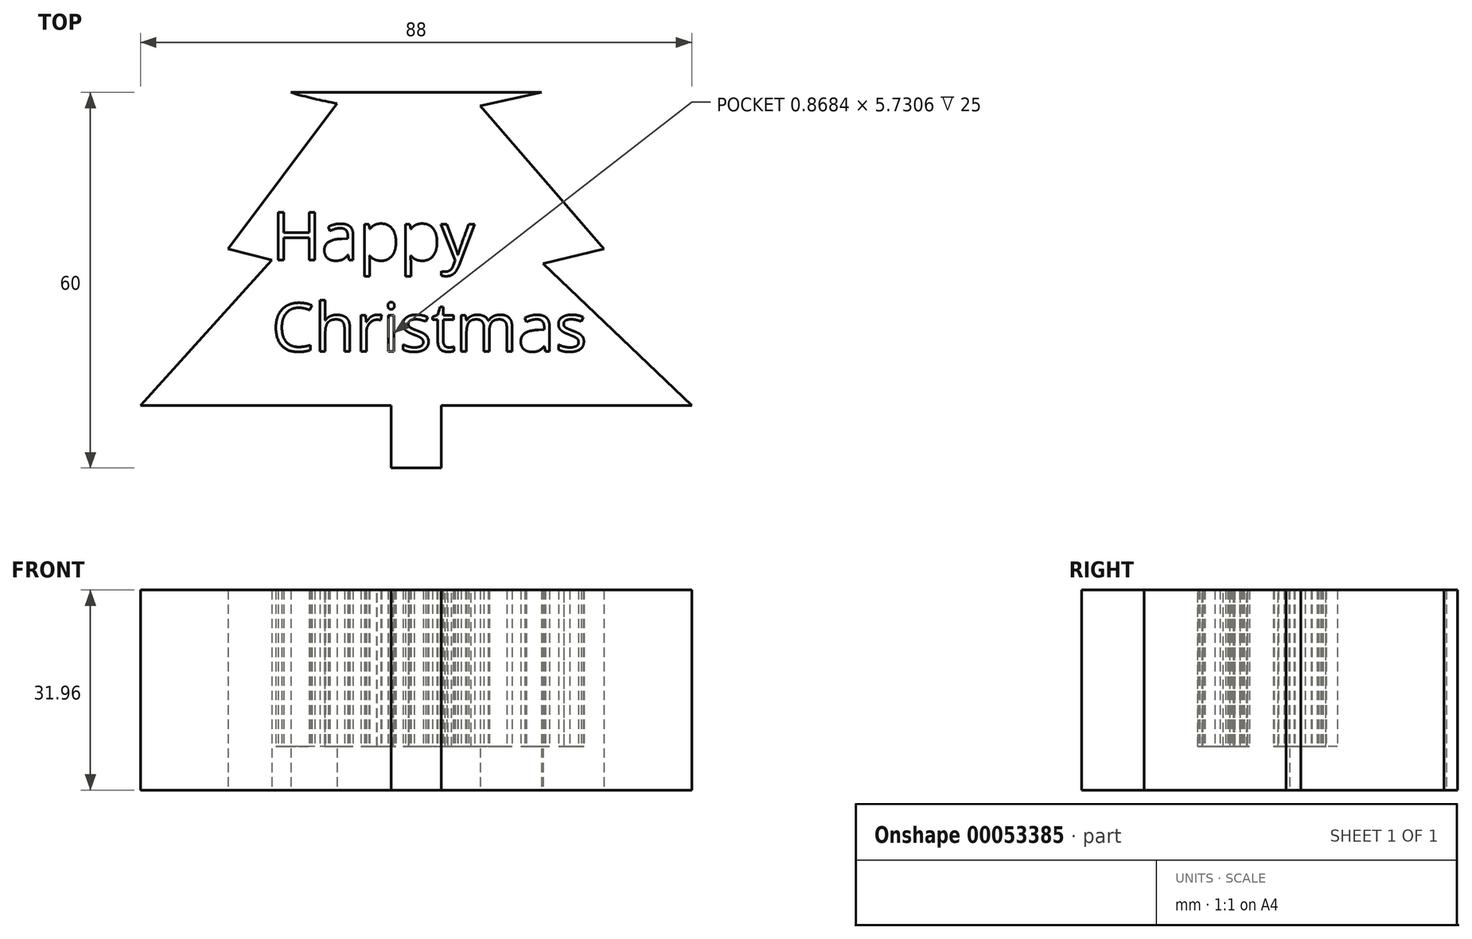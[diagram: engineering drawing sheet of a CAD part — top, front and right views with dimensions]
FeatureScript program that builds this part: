
annotation { "Feature Type Name" : "Feature", "Feature Type Description" : "" }
export const myFeature = defineFeature(function(context is Context, id is Id, definition is map)
    precondition{}
    {
        {
            var Q0;
            Q0=qCreatedBy(makeId("Top.planeOp"),FACE);
            var sketch = newSketch(context, id + "F0", { "sketchPlane" : qUnion([Q0])});
            skLineSegment(sketch, "E0", {"start": v(-16.3, -40.92) * mm, "end": v(-8.3, -40.92) * mm});
            skLineSegment(sketch, "E1", {"start": v(-8.3, -40.92) * mm, "end": v(-8.3, -30.92) * mm});
            skLineSegment(sketch, "E2", {"start": v(-16.3, -40.92) * mm, "end": v(-16.3, -30.92) * mm});
            skLineSegment(sketch, "E3", {"start": v(-16.3, -30.92) * mm, "end": v(-56.3, -30.92) * mm});
            skLineSegment(sketch, "E4", {"start": v(-8.3, -30.92) * mm, "end": v(31.7, -30.92) * mm});
            skLineSegment(sketch, "E5", {"start": v(-16.3, -30.92) * mm, "end": v(-8.3, -30.92) * mm});
            skLineSegment(sketch, "E6", {"start": v(-16.3, -30.92) * mm, "end": v(-12.3, -30.92) * mm});
            skLineSegment(sketch, "E7", {"start": v(-12.3, -30.92) * mm, "end": v(-12.3, 43.36) * mm});
            skLineSegment(sketch, "E8", {"start": v(-12.3, -30.92) * mm, "end": v(-12.3, -5.92) * mm});
            skLineSegment(sketch, "E9", {"start": v(-12.3, -5.92) * mm, "end": v(-12.3, 19.08) * mm});
            skLineSegment(sketch, "E10", {"start": v(-12.3, 19.08) * mm, "end": v(-12.3, 43.36) * mm});
            skLineSegment(sketch, "E11", {"start": v(-12.3, -5.92) * mm, "end": v(-42.3, -5.92) * mm});
            skLineSegment(sketch, "E12", {"start": v(-12.3, -5.92) * mm, "end": v(17.7, -5.92) * mm});
            skLineSegment(sketch, "E13", {"start": v(-12.3, 19.08) * mm, "end": v(-32.3, 19.08) * mm});
            skLineSegment(sketch, "E14", {"start": v(-12.3, 19.08) * mm, "end": v(7.7, 19.08) * mm});
            skArc(sketch, "E15", {"start": v(-32.3, 19.08) * mm, "mid": v(-12.3, 16.16) * mm, "end": v(7.7, 19.08) * mm});
            skArc(sketch, "E16", {"start": v(-42.3, -5.92) * mm, "mid": v(-12.3, -10.23) * mm, "end": v(17.7, -5.92) * mm});
            skLineSegment(sketch, "E17", {"start": v(-56.3, -30.92) * mm, "end": v(-35.34, -7.71) * mm});
            skLineSegment(sketch, "E18", {"start": v(-42.3, -5.92) * mm, "end": v(-24.92, 17.3) * mm});
            skArc(sketch, "E19", {"start": v(-12.32, 43.36) * mm, "mid": v(-12.31, 43.36) * mm, "end": v(-12.3, 43.36) * mm});
            skLineSegment(sketch, "E20", {"start": v(-42.3, -5.92) * mm, "end": v(-35.34, -7.71) * mm});
            skLineSegment(sketch, "E21", {"start": v(-32.3, 19.08) * mm, "end": v(-12.32, 43.36) * mm});
            skLineSegment(sketch, "E22", {"start": v(31.7, -30.92) * mm, "end": v(7.98, -8.28) * mm});
            skLineSegment(sketch, "E23", {"start": v(7.98, -8.28) * mm, "end": v(17.7, -5.92) * mm});
            skLineSegment(sketch, "E24", {"start": v(17.7, -5.92) * mm, "end": v(-2.06, 16.91) * mm});
            skLineSegment(sketch, "E25", {"start": v(-2.06, 16.91) * mm, "end": v(7.7, 19.08) * mm});
            skLineSegment(sketch, "E26", {"start": v(-12.3, 43.36) * mm, "end": v(7.7, 19.08) * mm});
            skSolve(sketch);
        }
        {
            var Q0;
            Q0=makeQuery(id+"F0.imprint","IMPRINT",FACE,{"disambiguationData":[TD([[makeQuery(id+"F0.imprint","IMPRINT",EDGE,{"derivedFrom":sQuery(id+"F0.wireOp",EDGE,"E10")}),1.0]])]});
            var Q1;
            Q1=makeQuery(id+"F0.imprint","IMPRINT",FACE,{"disambiguationData":[TD([[makeQuery(id+"F0.imprint","IMPRINT",EDGE,{"derivedFrom":sQuery(id+"F0.wireOp",EDGE,"E10")}),-1.0]])]});
            var Q2;
            {var subQ0=sQuery(id+"F0.wireOp",EDGE,"E13");Q2=makeQuery(id+"F0.imprint","IMPRINT",FACE,{"disambiguationData":[TD([[makeQuery(id+"F0.imprint","IMPRINT",EDGE,{"derivedFrom":subQ0}),1.0]])]});}
            var Q3;
            {var subQ0=sQuery(id+"F0.wireOp",EDGE,"E14");Q3=makeQuery(id+"F0.imprint","IMPRINT",FACE,{"disambiguationData":[TD([[makeQuery(id+"F0.imprint","IMPRINT",EDGE,{"derivedFrom":subQ0}),-1.0]])]});}
            var Q4;
            {var subQ0=sQuery(id+"F0.wireOp",EDGE,"E11");Q4=makeQuery(id+"F0.imprint","IMPRINT",FACE,{"disambiguationData":[TD([[makeQuery(id+"F0.imprint","IMPRINT",EDGE,{"derivedFrom":subQ0}),-1.0]])]});}
            var Q5;
            {var subQ0=sQuery(id+"F0.wireOp",EDGE,"E12");Q5=makeQuery(id+"F0.imprint","IMPRINT",FACE,{"disambiguationData":[TD([[makeQuery(id+"F0.imprint","IMPRINT",EDGE,{"derivedFrom":subQ0}),1.0]])]});}
            var Q6;
            {var subQ0=sQuery(id+"F0.wireOp",EDGE,"E11");Q6=makeQuery(id+"F0.imprint","IMPRINT",FACE,{"disambiguationData":[TD([[makeQuery(id+"F0.imprint","IMPRINT",EDGE,{"derivedFrom":subQ0}),1.0]])]});}
            var Q7;
            {var subQ0=sQuery(id+"F0.wireOp",EDGE,"E12");Q7=makeQuery(id+"F0.imprint","IMPRINT",FACE,{"disambiguationData":[TD([[makeQuery(id+"F0.imprint","IMPRINT",EDGE,{"derivedFrom":subQ0}),-1.0]])]});}
            var Q8;
            Q8=makeQuery(id+"F0.imprint","IMPRINT",FACE,{"disambiguationData":[TD([[makeQuery(id+"F0.imprint","IMPRINT",EDGE,{"derivedFrom":sQuery(id+"F0.wireOp",EDGE,"E3")}),-1.0]])]});
            var Q9;
            Q9=makeQuery(id+"F0.imprint","IMPRINT",FACE,{"disambiguationData":[TD([[makeQuery(id+"F0.imprint","IMPRINT",EDGE,{"derivedFrom":sQuery(id+"F0.wireOp",EDGE,"E4")}),1.0]])]});
            var Q10;
            Q10=makeQuery(id+"F0.imprint","IMPRINT",FACE,{"disambiguationData":[TD([[makeQuery(id+"F0.imprint","IMPRINT",EDGE,{"derivedFrom":sQuery(id+"F0.wireOp",EDGE,"E0")}),1.0]])]});
            extrude(context, id + "F1", {"entities" : qUnion([Q0, Q1, Q2, Q3, Q4, Q5, Q6, Q7, Q8, Q9, Q10]), "depth" : 6.96 * mm});
        }
        {
            var Q0;
            Q0=makeQuery(id+"F1.opExtrude","CAP_FACE",FACE,{"disambiguationData":[OSD([sQuery(id+"F0.wireOp",EDGE,"E0"),sQuery(id+"F0.wireOp",EDGE,"E1"),sQuery(id+"F0.wireOp",EDGE,"E2"),sQuery(id+"F0.wireOp",EDGE,"E3"),sQuery(id+"F0.wireOp",EDGE,"E4"),sQuery(id+"F0.wireOp",EDGE,"E15"),sQuery(id+"F0.wireOp",EDGE,"E17"),sQuery(id+"F0.wireOp",EDGE,"E18"),sQuery(id+"F0.wireOp",EDGE,"E19"),sQuery(id+"F0.wireOp",EDGE,"E20"),sQuery(id+"F0.wireOp",EDGE,"E21"),sQuery(id+"F0.wireOp",EDGE,"E22"),sQuery(id+"F0.wireOp",EDGE,"E23"),sQuery(id+"F0.wireOp",EDGE,"E24"),sQuery(id+"F0.wireOp",EDGE,"E25"),sQuery(id+"F0.wireOp",EDGE,"E26")])],"isStart":false});
            var sketch = newSketch(context, id + "F2", { "sketchPlane" : qUnion([Q0])});
            skText(sketch, "E27", { "text": "Happy \nChristmas", "fontName": "OpenSans-Regular.ttf"});
            const initialGuessF2  = {"E27": [-0.03534, -0.00771, 1, 0, 0.00771]};
            skSetInitialGuess(sketch, initialGuessF2);
            skSolve(sketch);
        }
        {
            var Q0;
            Q0=makeQuery(id+"F2.imprint","IMPRINT",FACE,{"disambiguationData":[TD([[makeQuery(id+"F2.imprint","IMPRINT",EDGE,{"derivedFrom":sQuery(id+"F2.wireOp",EDGE,"E27.sketch_text.stroke-0")}),1.0]])]});
            extrude(context, id + "F3", {"entities" : qUnion([Q0]), "operationType" : NewBodyOperationType.ADD, "depth" : 25 * mm});
        }
    });
